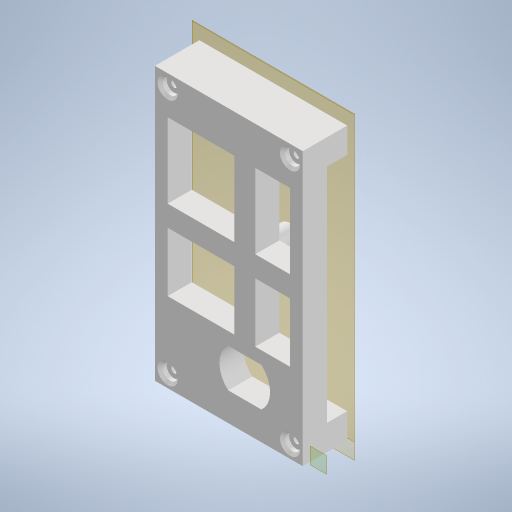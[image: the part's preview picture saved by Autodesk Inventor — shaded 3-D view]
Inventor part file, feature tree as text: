
AUTODESK INVENTOR PART (.ipt)
format: ipt  version: 2023 (Build 270158000, 158)  size: 450,048 bytes
history: native  units: mm
features: other x8, reference x7, plane x3, extrude x3, sketch x3, projected_geometry x2, chamfer x1
ambient origin geometry x8: Origin, YZ Plane, XZ Plane, XY Plane, X Axis, Y Axis, Z Axis, Center Point
bodies: Body1 (feature_tree)
feature tree (27):
  plane  "Work Plane1"
  plane  "Work Plane2"
  extrude  "Extrusion3"  Depth=0.1mm
  extrude  "Extrusion4"  Depth=10.0mm
  plane  "Work Plane3"
  extrude  "Extrusion5"  Depth=97.322mm
  chamfer  "Chamfer1"  Distance=48.171mm
  sketch  "Sketch3"  dims[d23=1.0mm d24=0.1mm]
  reference  "Reference6"
  reference  "Reference7"
  reference  "Reference8"
  reference  "Reference9"
  reference  "Reference10"
  sketch  "Sketch4"  dims[d25=0.1mm d26=10.0mm]
  reference  "Reference11"
  reference  "Reference12"
  projected_geometry  "Projected Loop2"
  sketch  "Sketch5"  dims[d27=10.0mm d28=2.5mm d29=20.0mm d31=48.171mm d32=20.0mm d34=97.322mm d37=8.0mm d38=0.0mm d39=0.1mm d40=5.0mm d41=5.0mm d42=5.0mm d43=5.0mm d44=9.5mm d45=0.0mm d46=6.0mm d47=20.0mm d49=48.171mm d50=20.0mm d52=97.322mm d55=26.25mm d56=0.0mm d57=1.0mm d58=2.0mm d59=45.0deg]
  projected_geometry  "Projected Loop3"
  parser-record x1  (decoder bookkeeping rows leaked as tree rows — omitted from the tree; the rows remain in map.json)
  other  "doorLockAssembly_V4.iam"
  other  "housingPlate:1"
  other  "rack_V3:1"
  other  "gear_V4:1"
  other  "BallBearing_8x22x7mm:1"
  other  "motor:1"
  other  "screw:1"
note: 1 file-system path scrubbed to <path> (originals preserved in map.json)
